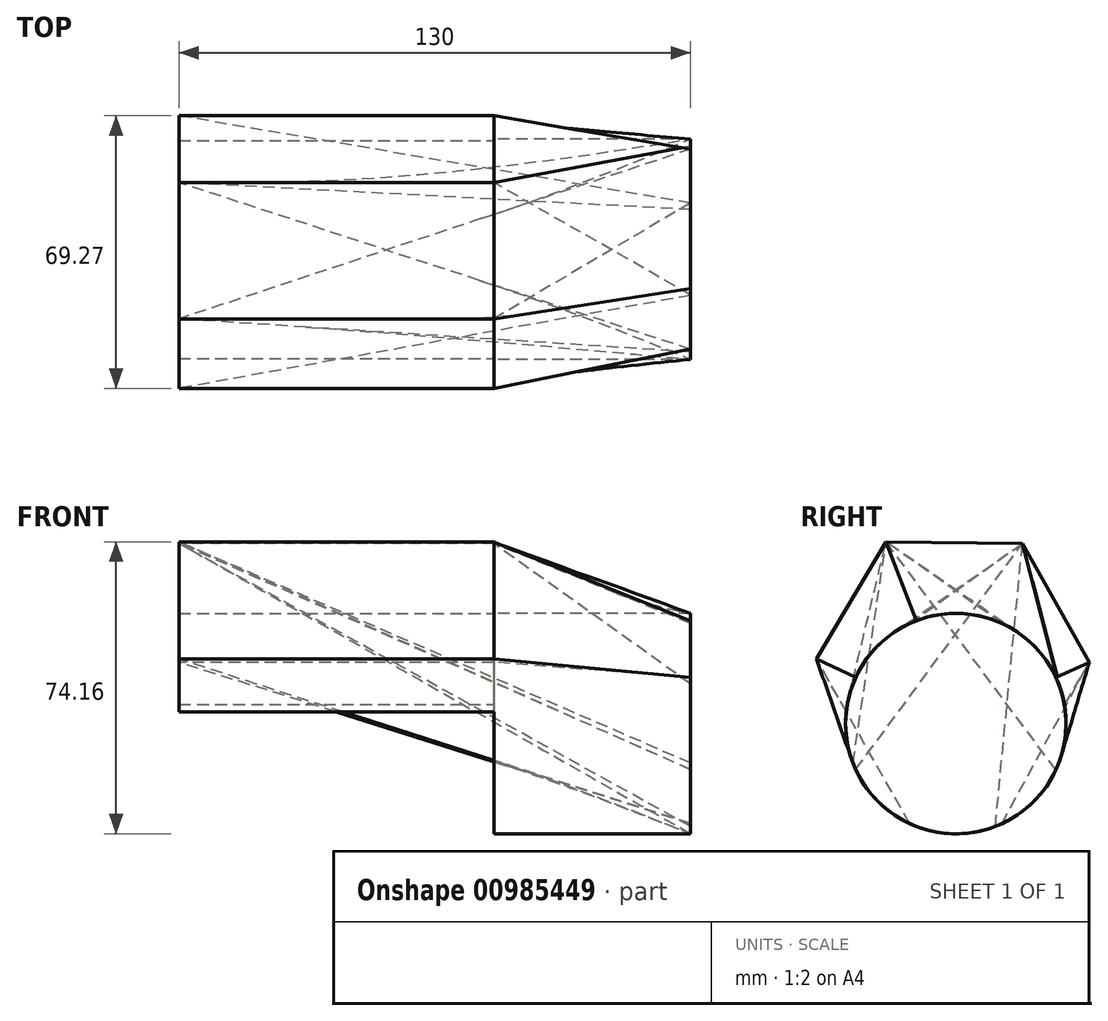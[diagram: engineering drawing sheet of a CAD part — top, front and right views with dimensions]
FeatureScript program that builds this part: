
annotation { "Feature Type Name" : "Feature", "Feature Type Description" : "" }
export const myFeature = defineFeature(function(context is Context, id is Id, definition is map)
    precondition{}
    {
        {
            var Q0;
            Q0=qCreatedBy(makeId("Right.planeOp"),FACE);
            var sketch = newSketch(context, id + "F0", { "sketchPlane" : qUnion([Q0])});
            skCircle(sketch, "E0.cCircle", {"center": v(-25.8, 18.43) * mm, "radius": 30 * mm, "construction": true});
            skLineSegment(sketch, "E0.0", {"start": v(8.83, 18.03) * mm, "end": v(-8.83, -11.77) * mm});
            skLineSegment(sketch, "E0.1", {"start": v(-8.83, -11.77) * mm, "end": v(-43.47, -11.37) * mm});
            skLineSegment(sketch, "E0.2", {"start": v(-43.47, -11.37) * mm, "end": v(-60.44, 18.83) * mm});
            skLineSegment(sketch, "E0.3", {"start": v(-60.44, 18.83) * mm, "end": v(-42.78, 48.63) * mm});
            skLineSegment(sketch, "E0.4", {"start": v(-42.78, 48.63) * mm, "end": v(-8.14, 48.23) * mm});
            skLineSegment(sketch, "E0.5", {"start": v(-8.14, 48.23) * mm, "end": v(8.83, 18.03) * mm});
            skPoint(sketch, "E0.0.midPoint", {"position": v(0, 3.13) * mm});
            skSolve(sketch);
        }
        {
            var Q0;
            Q0=makeQuery(id+"F0.imprint","IMPRINT",FACE,{"disambiguationData":[TD([[makeQuery(id+"F0.imprint","IMPRINT",EDGE,{"derivedFrom":sQuery(id+"F0.wireOp",EDGE,"E0.0")}),-1.0]])]});
            extrude(context, id + "F1", {"entities" : qUnion([Q0]), "depth" : 80 * mm, "offsetDistance" : 25 * mm});
        }
        {
            var Q0;
            Q0=makeQuery(id+"F1.opExtrude","CAP_FACE",FACE,{"disambiguationData":[OSD([sQuery(id+"F0.wireOp",EDGE,"E0.0"),sQuery(id+"F0.wireOp",EDGE,"E0.1"),sQuery(id+"F0.wireOp",EDGE,"E0.2"),sQuery(id+"F0.wireOp",EDGE,"E0.3"),sQuery(id+"F0.wireOp",EDGE,"E0.4"),sQuery(id+"F0.wireOp",EDGE,"E0.5")])],"isStart":false});
            var sketch = newSketch(context, id + "F2", { "sketchPlane" : qUnion([Q0])});
            skCircle(sketch, "E1", {"center": v(-25.06, 2.47) * mm, "radius": 28 * mm});
            skSolve(sketch);
        }
        {
            var Q0;
            {var subQ5=makeQuery(id+"F1.opExtrude","CAP_EDGE",EDGE,{"disambiguationData":[OSD([sQuery(id+"F0.wireOp",EDGE,"E0.1")])],"isStart":false});Q0=makeQuery(id+"F2.imprint","IMPRINT",FACE,{"disambiguationData":[TD([[makeQuery(id+"F2.imprint","IMPRINT",EDGE,{"derivedFrom":subQ5}),-1.0]])]});}
            extrude(context, id + "F3", {"entities" : qUnion([Q0]), "operationType" : NewBodyOperationType.REMOVE, "oppositeDirection" : true, "depth" : 80 * mm, "offsetDistance" : 25 * mm});
        }
        {
            var Q0;
            Q0 = qSketchRegion(id + "F2", true);
            extrude(context, id + "F4", {"entities" : qUnion([Q0]), "depth" : 50 * mm, "offsetDistance" : 25 * mm});
        }
        {
            var Q0;
            Q0=makeQuery(id+"F4.opExtrude","CAP_FACE",FACE,{"disambiguationData":[OSD([sQuery(id+"F2.wireOp",EDGE,"E1")])],"isStart":false});
            var Q1;
            Q1=makeQuery(id+"F1.opExtrude","SWEPT_FACE",FACE,{"disambiguationData":[OSD([sQuery(id+"F0.wireOp",EDGE,"E0.3")])]});
            loft(context, id + "F5", {"sheetProfilesArray" : [{ "sheetProfileEntities" : qUnion([Q0]) }, { "sheetProfileEntities" : qUnion([Q1]) }]});
        }
        {
            var Q0;
            Q0=makeQuery(id+"F4.opExtrude","CAP_FACE",FACE,{"disambiguationData":[OSD([sQuery(id+"F2.wireOp",EDGE,"E1")])],"isStart":false});
            var Q1;
            Q1=makeQuery(id+"F1.opExtrude","SWEPT_FACE",FACE,{"disambiguationData":[OSD([sQuery(id+"F0.wireOp",EDGE,"E0.4")])]});
            loft(context, id + "F6", {"sheetProfilesArray" : [{ "sheetProfileEntities" : qUnion([Q0]) }, { "sheetProfileEntities" : qUnion([Q1]) }]});
        }
        {
            var Q0;
            Q0=makeQuery(id+"F4.opExtrude","CAP_FACE",FACE,{"disambiguationData":[OSD([sQuery(id+"F2.wireOp",EDGE,"E1")])],"isStart":false});
            var Q1;
            Q1=makeQuery(id+"F1.opExtrude","SWEPT_FACE",FACE,{"disambiguationData":[OSD([sQuery(id+"F0.wireOp",EDGE,"E0.5")])]});
            loft(context, id + "F7", {"sheetProfilesArray" : [{ "sheetProfileEntities" : qUnion([Q0]) }, { "sheetProfileEntities" : qUnion([Q1]) }]});
        }
    });
